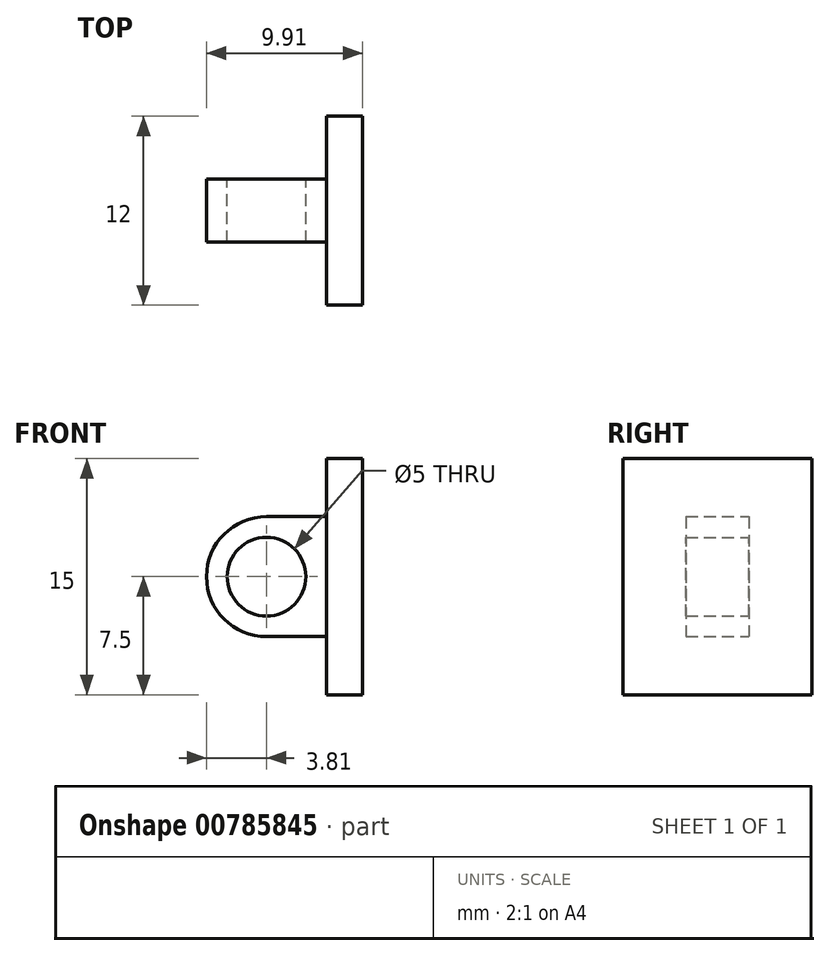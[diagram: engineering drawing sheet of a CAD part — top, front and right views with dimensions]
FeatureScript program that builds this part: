
annotation { "Feature Type Name" : "Feature", "Feature Type Description" : "" }
export const myFeature = defineFeature(function(context is Context, id is Id, definition is map)
    precondition{}
    {
        {
            var Q0;
            Q0=qCreatedBy(makeId("Front.planeOp"),FACE);
            var sketch = newSketch(context, id + "F0", { "sketchPlane" : qUnion([Q0])});
            skArc(sketch, "E0", {"start": v(0, 3.81) * mm, "mid": v(-3.81, 0) * mm, "end": v(0, -3.81) * mm});
            skCircle(sketch, "E1", {"center": v(0, 0) * mm, "radius": 2.5 * mm});
            skLineSegment(sketch, "E2", {"start": v(0, 3.81) * mm, "end": v(3.8, 3.81) * mm});
            skLineSegment(sketch, "E3", {"start": v(0, -3.81) * mm, "end": v(3.8, -3.81) * mm});
            skLineSegment(sketch, "E4", {"start": v(3.8, 3.81) * mm, "end": v(3.81, -3.81) * mm});
            skSolve(sketch);
        }
        {
            var Q0;
            Q0 = qSketchRegion(id + "F0", true);
            extrude(context, id + "F1", {"entities" : qUnion([Q0]), "depth" : 4 * mm, "offsetDistance" : 25.4 * mm});
        }
        {
            var Q0;
            Q0=makeQuery(id+"F1.opExtrude","SWEPT_FACE",FACE,{"disambiguationData":[OSD([sQuery(id+"F0.wireOp",EDGE,"E4")])]});
            var sketch = newSketch(context, id + "F2", { "sketchPlane" : qUnion([Q0])});
            skLineSegment(sketch, "E5.bottom", {"start": v(4, 7.5) * mm, "end": v(-8, 7.5) * mm});
            skLineSegment(sketch, "E5.top", {"start": v(4, -7.5) * mm, "end": v(-8, -7.5) * mm});
            skLineSegment(sketch, "E5.left", {"start": v(4, 7.5) * mm, "end": v(4, -7.5) * mm});
            skLineSegment(sketch, "E5.right", {"start": v(-8, 7.5) * mm, "end": v(-8, -7.5) * mm});
            skPoint(sketch, "E5.middle", {"position": v(-2, 0) * mm});
            skSolve(sketch);
        }
        {
            var Q0;
            Q0 = qSketchRegion(id + "F2", true);
            extrude(context, id + "F3", {"entities" : qUnion([Q0]), "operationType" : NewBodyOperationType.ADD, "depth" : 2.3 * mm, "offsetDistance" : 25.4 * mm});
        }
    });
